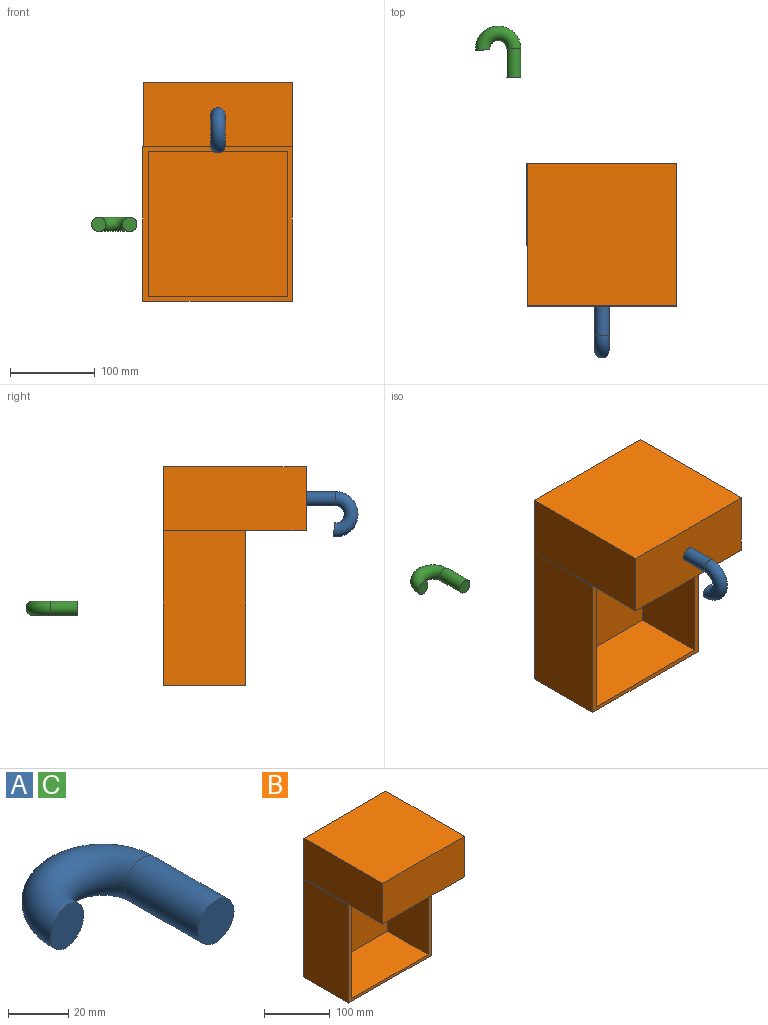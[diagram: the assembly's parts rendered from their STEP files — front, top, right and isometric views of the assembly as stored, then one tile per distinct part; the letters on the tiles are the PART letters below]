
ASSEMBLY  parts=3 mates=1
PART A: 4 faces, bbox 58.1x63.5x16.9 mm
  f0: plane 16.93x16.93mm, normal (0,-1,0), area 225mm2, adj f2
  f1: plane 16.93x16.86mm, normal (0.09,-1,0), area 225mm2, adj f3
  f2: cylinder r=8.46mm len=34.49mm, axis (0,1,0), area 1833.7mm2, adj f0,f3
  f3: torus R=18.36mm, axis (0,0,1), area 3151.1mm2, adj f1,f2
PART B: 17 faces, bbox 176.9x168.9x258.3 mm
  f0: plane 97.28x0.02mm, normal (0,0,1), area 2.3mm2, adj f3,f5,f6,f15
  f1: plane 182.63x97.28mm, normal (-1,0,0), area 17766.3mm2, adj f2,f4,f5,f6
  f2: plane 176.92x97.28mm, normal (0,0,-1), area 17211mm2, adj f1,f3,f5,f6
  f3: plane 182.63x97.28mm, normal (1,0,0), area 17766.3mm2, adj f0,f2,f5,f6
  f4: plane 97.28x0.58mm, normal (0,0,1), area 56.3mm2, adj f1,f5,f6,f13
  f5: plane 182.63x176.92mm, normal (0,-1,0), area 3975mm2, adj f0,f1,f2,f3,f4,f7,f8,f9
  f6: plane 258.32x176.92mm, normal (0,1,0), area 45655.8mm2, adj f0,f1,f2,f3,f4,f13,f15,f16
  f7: plane 172.39x87.12mm, normal (1,0,0), area 15019.2mm2, adj f5,f8,f10,f11
  f8: plane 164.36x87.12mm, normal (0,0,1), area 14319.7mm2, adj f5,f7,f9,f11
  f9: plane 172.39x87.12mm, normal (-1,0,0), area 15019.2mm2, adj f5,f8,f10,f11
  f10: plane 164.36x87.12mm, normal (0,0,-1), area 14319.7mm2, adj f5,f7,f9,f11
  f11: plane 172.39x164.36mm, normal (0,-1,0), area 28335.1mm2, adj f7,f8,f9,f10
  f12: plane 176.32x71.61mm, normal (0,0,-1), area 12625.2mm2, adj f5,f13,f14,f15
  f13: plane 168.89x75.69mm, normal (-1,0,0), area 12783.4mm2, adj f4,f6,f12,f14,f16
  f14: plane 176.32x75.69mm, normal (0,-1,0), area 13345.7mm2, adj f12,f13,f15,f16
  f15: plane 168.89x75.69mm, normal (1,0,0), area 12783.4mm2, adj f0,f6,f12,f14,f16
  f16: plane 176.32x168.89mm, normal (0,0,1), area 29777.6mm2, adj f6,f13,f14,f15
PART C: same geometry as A
PLACE A rot(axis=(0.71,0,0.71),180deg) t=(-14.29,-126.41,40.98)mm
PLACE B t=(-14.57,42.48,-88.18)mm
PLACE C t=(-118.43,143.43,-88.46)mm
MATE revolute A.f2 <-> B.f14  axis (0,-1,0) through (-14.29,-126.41,40.98)mm
